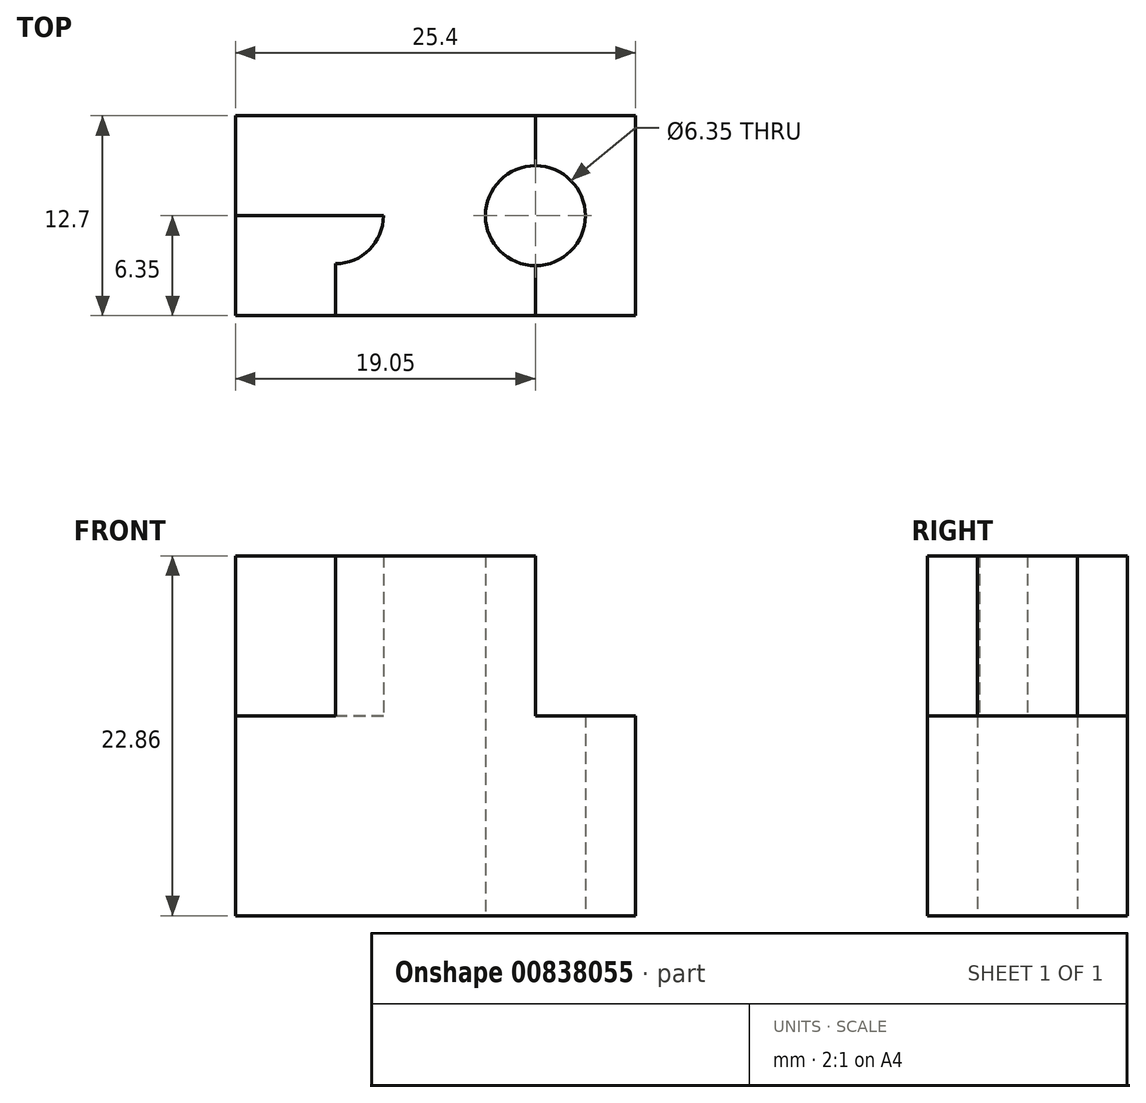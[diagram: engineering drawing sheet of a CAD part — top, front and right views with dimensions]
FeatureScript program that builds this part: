
annotation { "Feature Type Name" : "Feature", "Feature Type Description" : "" }
export const myFeature = defineFeature(function(context is Context, id is Id, definition is map)
    precondition{}
    {
        {
            var Q0;
            Q0=qCreatedBy(makeId("Top.planeOp"),FACE);
            var sketch = newSketch(context, id + "F0", { "sketchPlane" : qUnion([Q0])});
            skLineSegment(sketch, "E0.bottom", {"start": v(12.7, -6.35) * mm, "end": v(-12.7, -6.35) * mm});
            skLineSegment(sketch, "E0.top", {"start": v(12.7, 6.35) * mm, "end": v(-12.7, 6.35) * mm});
            skLineSegment(sketch, "E0.left", {"start": v(12.7, -6.35) * mm, "end": v(12.7, 6.35) * mm});
            skLineSegment(sketch, "E0.right", {"start": v(-12.7, -6.35) * mm, "end": v(-12.7, 6.35) * mm});
            skPoint(sketch, "E0.middle", {"position": v(0, 0) * mm});
            skLineSegment(sketch, "E1", {"start": v(-12.7, 0) * mm, "end": v(12.7, 0) * mm});
            skLineSegment(sketch, "E2", {"start": v(12.7, 0) * mm, "end": v(12.7, 0) * mm});
            skLineSegment(sketch, "E3.bottom", {"start": v(6.35, -6.35) * mm, "end": v(-6.35, -6.35) * mm});
            skLineSegment(sketch, "E3.top", {"start": v(6.35, 6.35) * mm, "end": v(-6.35, 6.35) * mm});
            skLineSegment(sketch, "E3.left", {"start": v(6.35, -6.35) * mm, "end": v(6.35, 6.35) * mm});
            skLineSegment(sketch, "E3.right", {"start": v(-6.35, -6.35) * mm, "end": v(-6.35, 6.35) * mm});
            skCircle(sketch, "E4", {"center": v(-6.35, 0) * mm, "radius": 3.05 * mm});
            skCircle(sketch, "E5", {"center": v(6.35, 0) * mm, "radius": 3.18 * mm});
            skSolve(sketch);
        }
        {
            var Q0;
            {var subQ1=sQuery(id+"F0.wireOp",EDGE,"E0.bottom");var subQ5=sQuery(id+"F0.wireOp",EDGE,"E3.left");var subQ6=makeQuery(id+"F0.imprint","INTERSECT",VERTEX,{"derivedFrom":[subQ1,subQ5]});Q0=makeQuery(id+"F0.imprint","IMPRINT",FACE,{"disambiguationData":[TD([[makeQuery(id+"F0.imprint","IMPRINT",EDGE,{"disambiguationData":[TD([[subQ6,-1.0]])],"derivedFrom":subQ1}),-1.0]])]});}
            var Q1;
            {var subQ3=sQuery(id+"F0.wireOp",EDGE,"E0.top");var subQ9=sQuery(id+"F0.wireOp",EDGE,"E3.left");var subQ10=makeQuery(id+"F0.imprint","INTERSECT",VERTEX,{"derivedFrom":[subQ3,subQ9]});Q1=makeQuery(id+"F0.imprint","IMPRINT",FACE,{"disambiguationData":[TD([[makeQuery(id+"F0.imprint","IMPRINT",EDGE,{"disambiguationData":[TD([[subQ10,-1.0]])],"derivedFrom":subQ3}),1.0]])]});}
            var Q2;
            {var subQ0=sQuery(id+"F0.wireOp",EDGE,"E3.left");var subQ1=sQuery(id+"F0.wireOp",EDGE,"E0.top");var subQ2=makeQuery(id+"F0.imprint","INTERSECT",VERTEX,{"derivedFrom":[subQ1,subQ0]});Q2=makeQuery(id+"F0.imprint","IMPRINT",FACE,{"disambiguationData":[TD([[makeQuery(id+"F0.imprint","IMPRINT",EDGE,{"disambiguationData":[TD([[subQ2,1.0]])],"derivedFrom":subQ1}),1.0]])]});}
            var Q3;
            {var subQ0=sQuery(id+"F0.wireOp",EDGE,"E3.left");var subQ1=sQuery(id+"F0.wireOp",EDGE,"E0.bottom");var subQ2=makeQuery(id+"F0.imprint","INTERSECT",VERTEX,{"derivedFrom":[subQ1,subQ0]});Q3=makeQuery(id+"F0.imprint","IMPRINT",FACE,{"disambiguationData":[TD([[makeQuery(id+"F0.imprint","IMPRINT",EDGE,{"disambiguationData":[TD([[subQ2,1.0]])],"derivedFrom":subQ1}),-1.0]])]});}
            var Q4;
            {var subQ3=sQuery(id+"F0.wireOp",EDGE,"E0.top");var subQ11=sQuery(id+"F0.wireOp",EDGE,"E3.left");var subQ12=makeQuery(id+"F0.imprint","INTERSECT",VERTEX,{"derivedFrom":[subQ3,subQ11]});var subQ15=sQuery(id+"F0.wireOp",EDGE,"E0.bottom");var subQ19=makeQuery(id+"F0.imprint","INTERSECT",VERTEX,{"derivedFrom":[subQ15,subQ11]});var subQ22=sQuery(id+"F0.wireOp",EDGE,"E0.right");var subQ26=makeQuery(id+"F0.imprint","INTERSECT",VERTEX,{"derivedFrom":[subQ3,subQ22]});var subQ32=makeQuery(id+"F0.imprint","INTERSECT",VERTEX,{"derivedFrom":[subQ15,subQ22]});Q4=qUnion([makeQuery(id+"F0.imprint","IMPRINT",FACE,{"disambiguationData":[TD([[makeQuery(id+"F0.imprint","IMPRINT",EDGE,{"disambiguationData":[TD([[subQ19,1.0]])],"derivedFrom":subQ15}),-1.0]])]}),makeQuery(id+"F0.imprint","IMPRINT",FACE,{"disambiguationData":[TD([[makeQuery(id+"F0.imprint","IMPRINT",EDGE,{"disambiguationData":[TD([[subQ32,1.0]])],"derivedFrom":subQ15}),-1.0]])]}),makeQuery(id+"F0.imprint","IMPRINT",FACE,{"disambiguationData":[TD([[makeQuery(id+"F0.imprint","IMPRINT",EDGE,{"disambiguationData":[TD([[subQ12,1.0]])],"derivedFrom":subQ3}),1.0]])]}),makeQuery(id+"F0.imprint","IMPRINT",FACE,{"disambiguationData":[TD([[makeQuery(id+"F0.imprint","IMPRINT",EDGE,{"disambiguationData":[TD([[subQ26,1.0]])],"derivedFrom":subQ3}),1.0]])]}),makeQuery(id+"F0.imprint","IMPRINT",FACE,{"disambiguationData":[TD([[makeQuery(id+"F0.imprint","IMPRINT",EDGE,{"disambiguationData":[TD([[subQ19,-1.0]])],"derivedFrom":subQ15}),-1.0]])]}),makeQuery(id+"F0.imprint","IMPRINT",FACE,{"disambiguationData":[TD([[makeQuery(id+"F0.imprint","IMPRINT",EDGE,{"disambiguationData":[TD([[subQ12,-1.0]])],"derivedFrom":subQ3}),1.0]])]})]);}
            var Q5;
            {var subQ1=sQuery(id+"F0.wireOp",EDGE,"E0.right");var subQ6=sQuery(id+"F0.wireOp",EDGE,"E0.bottom");var subQ9=makeQuery(id+"F0.imprint","INTERSECT",VERTEX,{"derivedFrom":[subQ6,subQ1]});Q5=makeQuery(id+"F0.imprint","IMPRINT",FACE,{"disambiguationData":[TD([[makeQuery(id+"F0.imprint","IMPRINT",EDGE,{"disambiguationData":[TD([[subQ9,1.0]])],"derivedFrom":subQ6}),-1.0]])]});}
            var Q6;
            {var subQ3=sQuery(id+"F0.wireOp",EDGE,"E0.top");var subQ6=sQuery(id+"F0.wireOp",EDGE,"E0.right");var subQ9=makeQuery(id+"F0.imprint","INTERSECT",VERTEX,{"derivedFrom":[subQ3,subQ6]});Q6=makeQuery(id+"F0.imprint","IMPRINT",FACE,{"disambiguationData":[TD([[makeQuery(id+"F0.imprint","IMPRINT",EDGE,{"disambiguationData":[TD([[subQ9,1.0]])],"derivedFrom":subQ3}),1.0]])]});}
            var Q7;
            {var subQ0=sQuery(id+"F0.wireOp",EDGE,"E4");var subQ1=sQuery(id+"F0.wireOp",EDGE,"E1");var subQ2=makeQuery(id+"F0.imprint","INTERSECT",VERTEX,{"disambiguationData":[OD(0.0)],"derivedFrom":[subQ1,subQ0]});Q7=makeQuery(id+"F0.imprint","IMPRINT",FACE,{"disambiguationData":[TD([[makeQuery(id+"F0.imprint","IMPRINT",EDGE,{"disambiguationData":[TD([[subQ2,1.0]])],"derivedFrom":subQ1}),1.0]])]});}
            var Q8;
            {var subQ0=sQuery(id+"F0.wireOp",EDGE,"E3.right");var subQ1=sQuery(id+"F0.wireOp",EDGE,"E1");var subQ2=makeQuery(id+"F0.imprint","INTERSECT",VERTEX,{"derivedFrom":[subQ1,subQ0]});Q8=makeQuery(id+"F0.imprint","IMPRINT",FACE,{"disambiguationData":[TD([[makeQuery(id+"F0.imprint","IMPRINT",EDGE,{"disambiguationData":[TD([[subQ2,1.0]])],"derivedFrom":subQ1}),1.0]])]});}
            var Q9;
            {var subQ0=sQuery(id+"F0.wireOp",EDGE,"E3.right");var subQ1=sQuery(id+"F0.wireOp",EDGE,"E1");var subQ2=makeQuery(id+"F0.imprint","INTERSECT",VERTEX,{"derivedFrom":[subQ1,subQ0]});Q9=makeQuery(id+"F0.imprint","IMPRINT",FACE,{"disambiguationData":[TD([[makeQuery(id+"F0.imprint","IMPRINT",EDGE,{"disambiguationData":[TD([[subQ2,1.0]])],"derivedFrom":subQ1}),-1.0]])]});}
            var Q10;
            {var subQ0=sQuery(id+"F0.wireOp",EDGE,"E4");var subQ1=sQuery(id+"F0.wireOp",EDGE,"E1");var subQ2=makeQuery(id+"F0.imprint","INTERSECT",VERTEX,{"disambiguationData":[OD(0.0)],"derivedFrom":[subQ1,subQ0]});Q10=makeQuery(id+"F0.imprint","IMPRINT",FACE,{"disambiguationData":[TD([[makeQuery(id+"F0.imprint","IMPRINT",EDGE,{"disambiguationData":[TD([[subQ2,1.0]])],"derivedFrom":subQ1}),-1.0]])]});}
            extrude(context, id + "F1", {"entities" : qUnion([Q0, Q1, Q2, Q3, Q4, Q5, Q6, Q7, Q8, Q9, Q10]), "depth" : 12.7 * mm, "offsetDistance" : 25.4 * mm});
        }
        {
            var Q0;
            Q0=makeQuery(id+"F1.opExtrude","CAP_FACE",FACE,{"disambiguationData":[OSD([sQuery(id+"F0.wireOp",EDGE,"E0.bottom"),sQuery(id+"F0.wireOp",EDGE,"E0.top"),sQuery(id+"F0.wireOp",EDGE,"E0.left"),sQuery(id+"F0.wireOp",EDGE,"E0.right"),sQuery(id+"F0.wireOp",EDGE,"E5")])],"isStart":false});
            var sketch = newSketch(context, id + "F2", { "sketchPlane" : qUnion([Q0])});
            skLineSegment(sketch, "E6.bottom", {"start": v(6.35, -6.35) * mm, "end": v(-6.35, -6.35) * mm});
            skLineSegment(sketch, "E6.top", {"start": v(6.35, 6.35) * mm, "end": v(-6.35, 6.35) * mm});
            skLineSegment(sketch, "E6.left", {"start": v(6.35, -6.35) * mm, "end": v(6.35, 6.35) * mm});
            skLineSegment(sketch, "E6.right", {"start": v(-6.35, -6.35) * mm, "end": v(-6.35, 6.35) * mm});
            skPoint(sketch, "E6.middle", {"position": v(0, 0) * mm});
            skLineSegment(sketch, "E7", {"start": v(0, 0) * mm, "end": v(-12.7, 0) * mm});
            skCircle(sketch, "E8", {"center": v(-6.35, 0) * mm, "radius": 3.05 * mm});
            skSolve(sketch);
        }
        {
            var Q0;
            {var subQ0=sQuery(id+"F2.wireOp",EDGE,"E8");var subQ1=sQuery(id+"F2.wireOp",EDGE,"E6.right");var subQ2=makeQuery(id+"F2.imprint","INTERSECT",VERTEX,{"disambiguationData":[OD(0.0)],"derivedFrom":[subQ1,subQ0]});Q0=makeQuery(id+"F2.imprint","IMPRINT",FACE,{"disambiguationData":[TD([[makeQuery(id+"F2.imprint","IMPRINT",EDGE,{"disambiguationData":[TD([[subQ2,-1.0]])],"derivedFrom":subQ1}),-1.0]])]});}
            var Q1;
            {var subQ0=sQuery(id+"F2.wireOp",EDGE,"E7");var subQ1=sQuery(id+"F2.wireOp",EDGE,"E6.right");var subQ2=makeQuery(id+"F2.imprint","INTERSECT",VERTEX,{"derivedFrom":[subQ1,subQ0]});Q1=makeQuery(id+"F2.imprint","IMPRINT",FACE,{"disambiguationData":[TD([[makeQuery(id+"F2.imprint","IMPRINT",EDGE,{"disambiguationData":[TD([[subQ2,-1.0]])],"derivedFrom":subQ1}),-1.0]])]});}
            var Q2;
            {var subQ0=sQuery(id+"F2.wireOp",EDGE,"E8");var subQ1=sQuery(id+"F2.wireOp",EDGE,"E6.right");var subQ2=makeQuery(id+"F2.imprint","INTERSECT",VERTEX,{"disambiguationData":[OD(0.0)],"derivedFrom":[subQ1,subQ0]});Q2=makeQuery(id+"F2.imprint","IMPRINT",FACE,{"disambiguationData":[TD([[makeQuery(id+"F2.imprint","IMPRINT",EDGE,{"disambiguationData":[TD([[subQ2,-1.0]])],"derivedFrom":subQ1}),1.0]])]});}
            var Q3;
            {var subQ0=sQuery(id+"F2.wireOp",EDGE,"E7");var subQ1=sQuery(id+"F2.wireOp",EDGE,"E6.right");var subQ2=makeQuery(id+"F2.imprint","INTERSECT",VERTEX,{"derivedFrom":[subQ1,subQ0]});Q3=makeQuery(id+"F2.imprint","IMPRINT",FACE,{"disambiguationData":[TD([[makeQuery(id+"F2.imprint","IMPRINT",EDGE,{"disambiguationData":[TD([[subQ2,-1.0]])],"derivedFrom":subQ1}),1.0]])]});}
            var Q4;
            Q4=sQuery(id+"F2.wireOp",EDGE,"E8");
            extrude(context, id + "F3", {"entities" : qUnion([Q0, Q1, Q2, Q3]), "operationType" : NewBodyOperationType.ADD, "surfaceEntities" : qUnion([Q4]), "depth" : 10.16 * mm, "offsetDistance" : 25.4 * mm});
        }
    });
